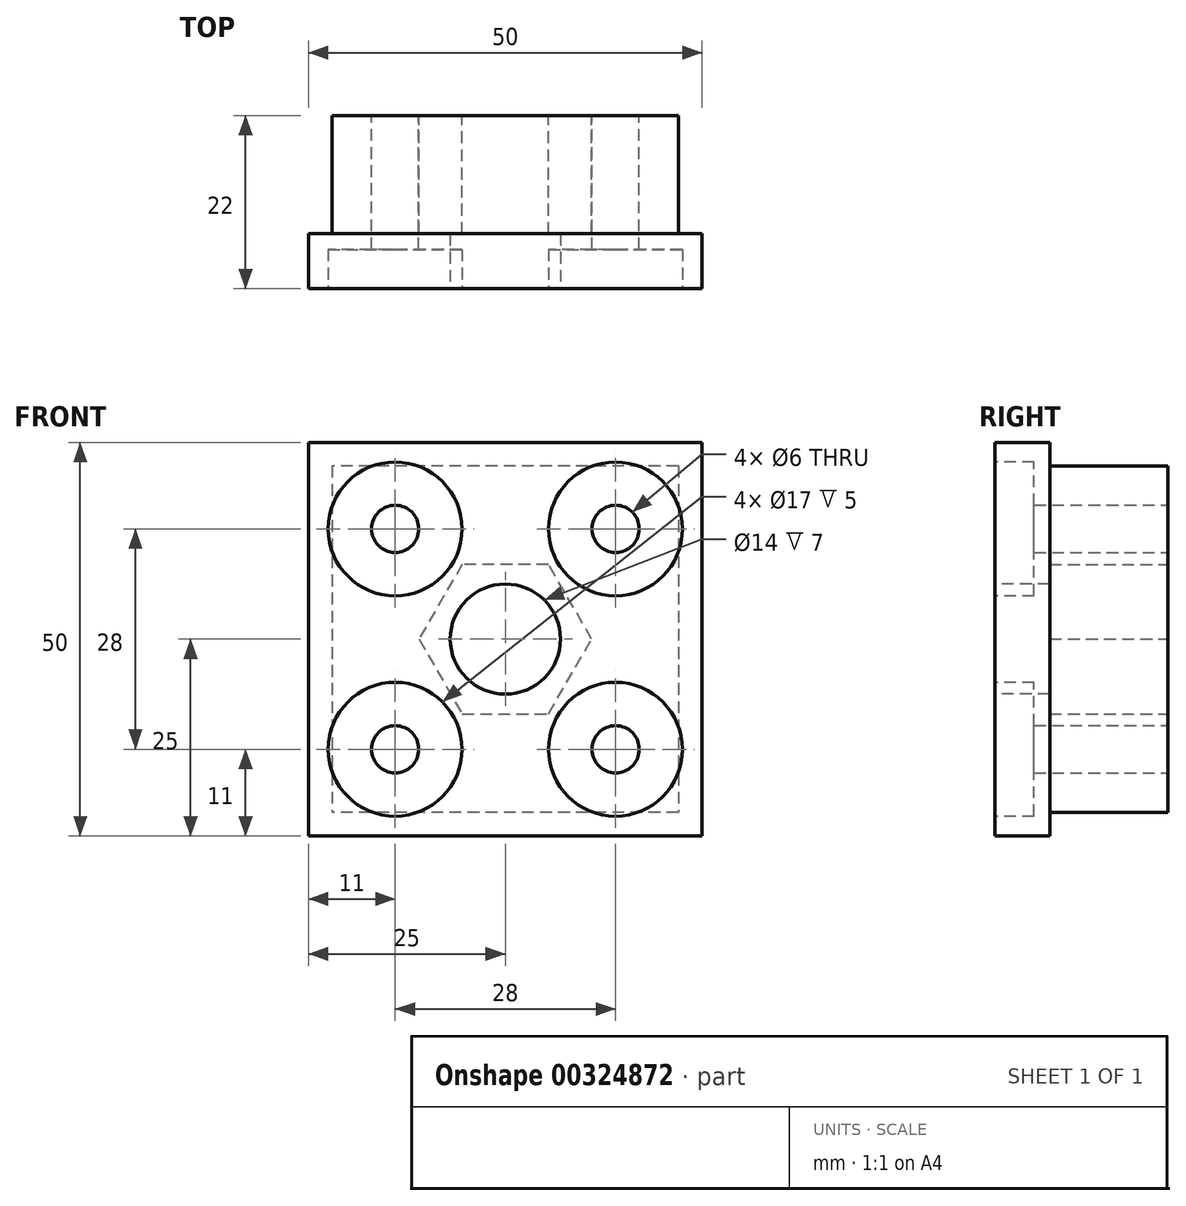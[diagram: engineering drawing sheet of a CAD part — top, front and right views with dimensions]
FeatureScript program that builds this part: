
annotation { "Feature Type Name" : "Feature", "Feature Type Description" : "" }
export const myFeature = defineFeature(function(context is Context, id is Id, definition is map)
    precondition{}
    {
        {
            var Q0;
            Q0=qCreatedBy(makeId("Front.planeOp"),FACE);
            var sketch = newSketch(context, id + "F0", { "sketchPlane" : qUnion([Q0])});
            skLineSegment(sketch, "E0.bottom", {"start": v(-25, 25) * mm, "end": v(25, 25) * mm});
            skLineSegment(sketch, "E0.top", {"start": v(-25, -25) * mm, "end": v(25, -25) * mm});
            skLineSegment(sketch, "E0.left", {"start": v(-25, 25) * mm, "end": v(-25, -25) * mm});
            skLineSegment(sketch, "E0.right", {"start": v(25, 25) * mm, "end": v(25, -25) * mm});
            skPoint(sketch, "E0.middle", {"position": v(0, 0) * mm});
            skSolve(sketch);
        }
        {
            var Q0;
            Q0=makeQuery(id+"F0.imprint","IMPRINT",FACE,{"disambiguationData":[TD([[makeQuery(id+"F0.imprint","IMPRINT",EDGE,{"derivedFrom":sQuery(id+"F0.wireOp",EDGE,"E0.bottom")}),-1.0]])]});
            extrude(context, id + "F1", {"entities" : qUnion([Q0]), "oppositeDirection" : true, "depth" : 7 * mm});
        }
        {
            var Q0;
            Q0=makeQuery(id+"F1.opExtrude","CAP_FACE",FACE,{"disambiguationData":[OSD([sQuery(id+"F0.wireOp",EDGE,"E0.bottom"),sQuery(id+"F0.wireOp",EDGE,"E0.top"),sQuery(id+"F0.wireOp",EDGE,"E0.left"),sQuery(id+"F0.wireOp",EDGE,"E0.right")])],"isStart":false});
            var sketch = newSketch(context, id + "F2", { "sketchPlane" : qUnion([Q0])});
            skLineSegment(sketch, "E1.bottom", {"start": v(-22, 22) * mm, "end": v(22, 22) * mm});
            skLineSegment(sketch, "E1.top", {"start": v(-22, -22) * mm, "end": v(22, -22) * mm});
            skLineSegment(sketch, "E1.left", {"start": v(-22, 22) * mm, "end": v(-22, -22) * mm});
            skLineSegment(sketch, "E1.right", {"start": v(22, 22) * mm, "end": v(22, -22) * mm});
            skPoint(sketch, "E1.middle", {"position": v(0, 0) * mm});
            skSolve(sketch);
        }
        {
            var Q0;
            Q0=makeQuery(id+"F2.imprint","IMPRINT",FACE,{"disambiguationData":[TD([[makeQuery(id+"F2.imprint","IMPRINT",EDGE,{"derivedFrom":sQuery(id+"F2.wireOp",EDGE,"E1.bottom")}),-1.0]])]});
            extrude(context, id + "F3", {"entities" : qUnion([Q0]), "operationType" : NewBodyOperationType.ADD, "depth" : 15 * mm});
        }
        {
            var Q0;
            Q0=makeQuery(id+"F3.opExtrude","CAP_FACE",FACE,{"disambiguationData":[OSD([sQuery(id+"F2.wireOp",EDGE,"E1.bottom"),sQuery(id+"F2.wireOp",EDGE,"E1.top"),sQuery(id+"F2.wireOp",EDGE,"E1.left"),sQuery(id+"F2.wireOp",EDGE,"E1.right")])],"isStart":false});
            var sketch = newSketch(context, id + "F4", { "sketchPlane" : qUnion([Q0])});
            skLineSegment(sketch, "E2", {"start": v(-22, 22) * mm, "end": v(22, -22) * mm, "construction": true});
            skLineSegment(sketch, "E3", {"start": v(22, 22) * mm, "end": v(-22, -22) * mm, "construction": true});
            skLineSegment(sketch, "E4.bottom", {"start": v(-14, 14) * mm, "end": v(14, 14) * mm, "construction": true});
            skLineSegment(sketch, "E4.top", {"start": v(-14, -14) * mm, "end": v(14, -14) * mm, "construction": true});
            skLineSegment(sketch, "E4.left", {"start": v(-14, 14) * mm, "end": v(-14, -14) * mm, "construction": true});
            skLineSegment(sketch, "E4.right", {"start": v(14, 14) * mm, "end": v(14, -14) * mm, "construction": true});
            skPoint(sketch, "E4.middle", {"position": v(0, 0) * mm});
            skCircle(sketch, "E5", {"center": v(-14, 14) * mm, "radius": 3 * mm});
            skCircle(sketch, "E6", {"center": v(14, 14) * mm, "radius": 3 * mm});
            skCircle(sketch, "E7", {"center": v(-14, -14) * mm, "radius": 3 * mm});
            skCircle(sketch, "E8", {"center": v(14, -14) * mm, "radius": 3 * mm});
            skSolve(sketch);
        }
        {
            var Q0;
            Q0=makeQuery(id+"F4.imprint","IMPRINT",FACE,{"disambiguationData":[TD([[makeQuery(id+"F4.imprint","IMPRINT",EDGE,{"derivedFrom":sQuery(id+"F4.wireOp",EDGE,"E5")}),1.0]])]});
            var Q1;
            Q1=makeQuery(id+"F4.imprint","IMPRINT",FACE,{"disambiguationData":[TD([[makeQuery(id+"F4.imprint","IMPRINT",EDGE,{"derivedFrom":sQuery(id+"F4.wireOp",EDGE,"E6")}),1.0]])]});
            var Q2;
            Q2=makeQuery(id+"F4.imprint","IMPRINT",FACE,{"disambiguationData":[TD([[makeQuery(id+"F4.imprint","IMPRINT",EDGE,{"derivedFrom":sQuery(id+"F4.wireOp",EDGE,"E8")}),1.0]])]});
            var Q3;
            Q3=makeQuery(id+"F4.imprint","IMPRINT",FACE,{"disambiguationData":[TD([[makeQuery(id+"F4.imprint","IMPRINT",EDGE,{"derivedFrom":sQuery(id+"F4.wireOp",EDGE,"E7")}),1.0]])]});
            var Q4;
            Q4=makeQuery(id+"F4.imprint","IMPRINT",FACE,{"disambiguationData":[TD([[makeQuery(id+"F4.imprint","IMPRINT",EDGE,{"derivedFrom":sQuery(id+"F4.wireOp",EDGE,"QwKJkzou-eQ0R-DmLM-VaWs-TZL8aThNHikG")}),1.0]])]});
            extrude(context, id + "F5", {"entities" : qUnion([Q0, Q1, Q2, Q3, Q4]), "operationType" : NewBodyOperationType.REMOVE, "oppositeDirection" : true, "depth" : 25 * mm});
        }
        {
            var Q0;
            Q0=makeQuery(id+"F1.opExtrude","CAP_FACE",FACE,{"disambiguationData":[OSD([sQuery(id+"F0.wireOp",EDGE,"E0.bottom"),sQuery(id+"F0.wireOp",EDGE,"E0.top"),sQuery(id+"F0.wireOp",EDGE,"E0.left"),sQuery(id+"F0.wireOp",EDGE,"E0.right")])],"isStart":true});
            var sketch = newSketch(context, id + "F6", { "sketchPlane" : qUnion([Q0])});
            skCircle(sketch, "E9", {"center": v(-14, 14) * mm, "radius": 8.5 * mm});
            skPoint(sketch, "E10.center", {"position": v(6, -6) * mm});
            skCircle(sketch, "E11.1.0", {"center": v(-14, -14) * mm, "radius": 8.5 * mm});
            skCircle(sketch, "E11.2.0", {"center": v(14, -14) * mm, "radius": 8.5 * mm});
            skCircle(sketch, "E11.3.0", {"center": v(14, 14) * mm, "radius": 8.5 * mm});
            skPoint(sketch, "E11.center", {"position": v(0, 0) * mm});
            skSolve(sketch);
        }
        {
            var Q0;
            Q0=makeQuery(id+"F1.opExtrude","CAP_FACE",FACE,{"disambiguationData":[OSD([sQuery(id+"F0.wireOp",EDGE,"E0.bottom"),sQuery(id+"F0.wireOp",EDGE,"E0.top"),sQuery(id+"F0.wireOp",EDGE,"E0.left"),sQuery(id+"F0.wireOp",EDGE,"E0.right")])],"isStart":true});
            var sketch = newSketch(context, id + "F7", { "sketchPlane" : qUnion([Q0])});
            skCircle(sketch, "E12", {"center": v(0, 0) * mm, "radius": 7 * mm});
            skSolve(sketch);
        }
        {
            var Q0;
            Q0=makeQuery(id+"F7.imprint","IMPRINT",FACE,{"disambiguationData":[TD([[makeQuery(id+"F7.imprint","IMPRINT",EDGE,{"derivedFrom":sQuery(id+"F7.wireOp",EDGE,"E12")}),1.0]])]});
            extrude(context, id + "F8", {"entities" : qUnion([Q0]), "operationType" : NewBodyOperationType.REMOVE, "oppositeDirection" : true, "depth" : 25 * mm});
        }
        {
            var Q0;
            Q0=makeQuery(id+"F3.opExtrude","CAP_FACE",FACE,{"disambiguationData":[OSD([sQuery(id+"F2.wireOp",EDGE,"E1.bottom"),sQuery(id+"F2.wireOp",EDGE,"E1.top"),sQuery(id+"F2.wireOp",EDGE,"E1.left"),sQuery(id+"F2.wireOp",EDGE,"E1.right")])],"isStart":false});
            var sketch = newSketch(context, id + "F9", { "sketchPlane" : qUnion([Q0])});
            skCircle(sketch, "E13.cCircle", {"center": v(0, 0) * mm, "radius": 9.5 * mm, "construction": true});
            skLineSegment(sketch, "E13.0", {"start": v(5.48, -9.5) * mm, "end": v(-5.48, -9.5) * mm});
            skLineSegment(sketch, "E13.1", {"start": v(-5.48, -9.5) * mm, "end": v(-10.97, 0) * mm});
            skLineSegment(sketch, "E13.2", {"start": v(-10.97, 0) * mm, "end": v(-5.48, 9.5) * mm});
            skLineSegment(sketch, "E13.3", {"start": v(-5.48, 9.5) * mm, "end": v(5.48, 9.5) * mm});
            skLineSegment(sketch, "E13.4", {"start": v(5.48, 9.5) * mm, "end": v(10.97, 0) * mm});
            skLineSegment(sketch, "E13.5", {"start": v(10.97, 0) * mm, "end": v(5.48, -9.5) * mm});
            skPoint(sketch, "E13.0.midPoint", {"position": v(0, -9.5) * mm});
            skSolve(sketch);
        }
        {
            var Q0;
            Q0=makeQuery(id+"F9.imprint","IMPRINT",FACE,{"disambiguationData":[TD([[makeQuery(id+"F9.imprint","IMPRINT",EDGE,{"derivedFrom":sQuery(id+"F9.wireOp",EDGE,"E13.0")}),-1.0]])]});
            extrude(context, id + "F10", {"entities" : qUnion([Q0]), "operationType" : NewBodyOperationType.REMOVE, "oppositeDirection" : true, "depth" : 15 * mm});
        }
        {
            var Q0;
            Q0 = qSketchRegion(id + "F6", true);
            extrude(context, id + "F11", {"entities" : qUnion([Q0]), "operationType" : NewBodyOperationType.REMOVE, "oppositeDirection" : true, "depth" : 5 * mm});
        }
    });
